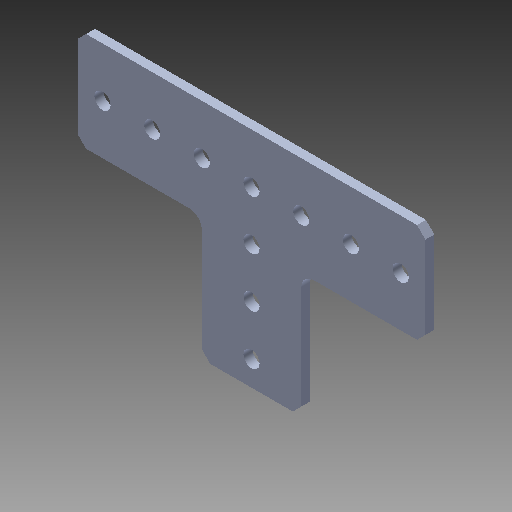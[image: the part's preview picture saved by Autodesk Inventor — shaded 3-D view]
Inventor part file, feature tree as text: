
AUTODESK INVENTOR PART (.ipt)
format: ipt  version: 2017 (Build 210142000, 142)  size: 139,264 bytes
history: native  units: in
note: dims shown in document units (in); Inventor stores cm internally (conversion verified against a paired STEP export)
features: fillet x1, other x1, imported_body x1
ambient origin geometry x8: Origin, YZ Plane, XZ Plane, XY Plane, X Axis, Y Axis, Z Axis, Center Point
bodies: Body1 (feature_tree)
feature tree (3):
  fillet  "Fillet1"  [1 undecoded]
  other  "VersaFrame Short Gusset1"
  imported_body  "Base1"
note: 1 required parameter value undecoded (feature->parameter linkage not recoverable at this tier; creation-order binding heuristic only, values carry confidence <= 0.55)
